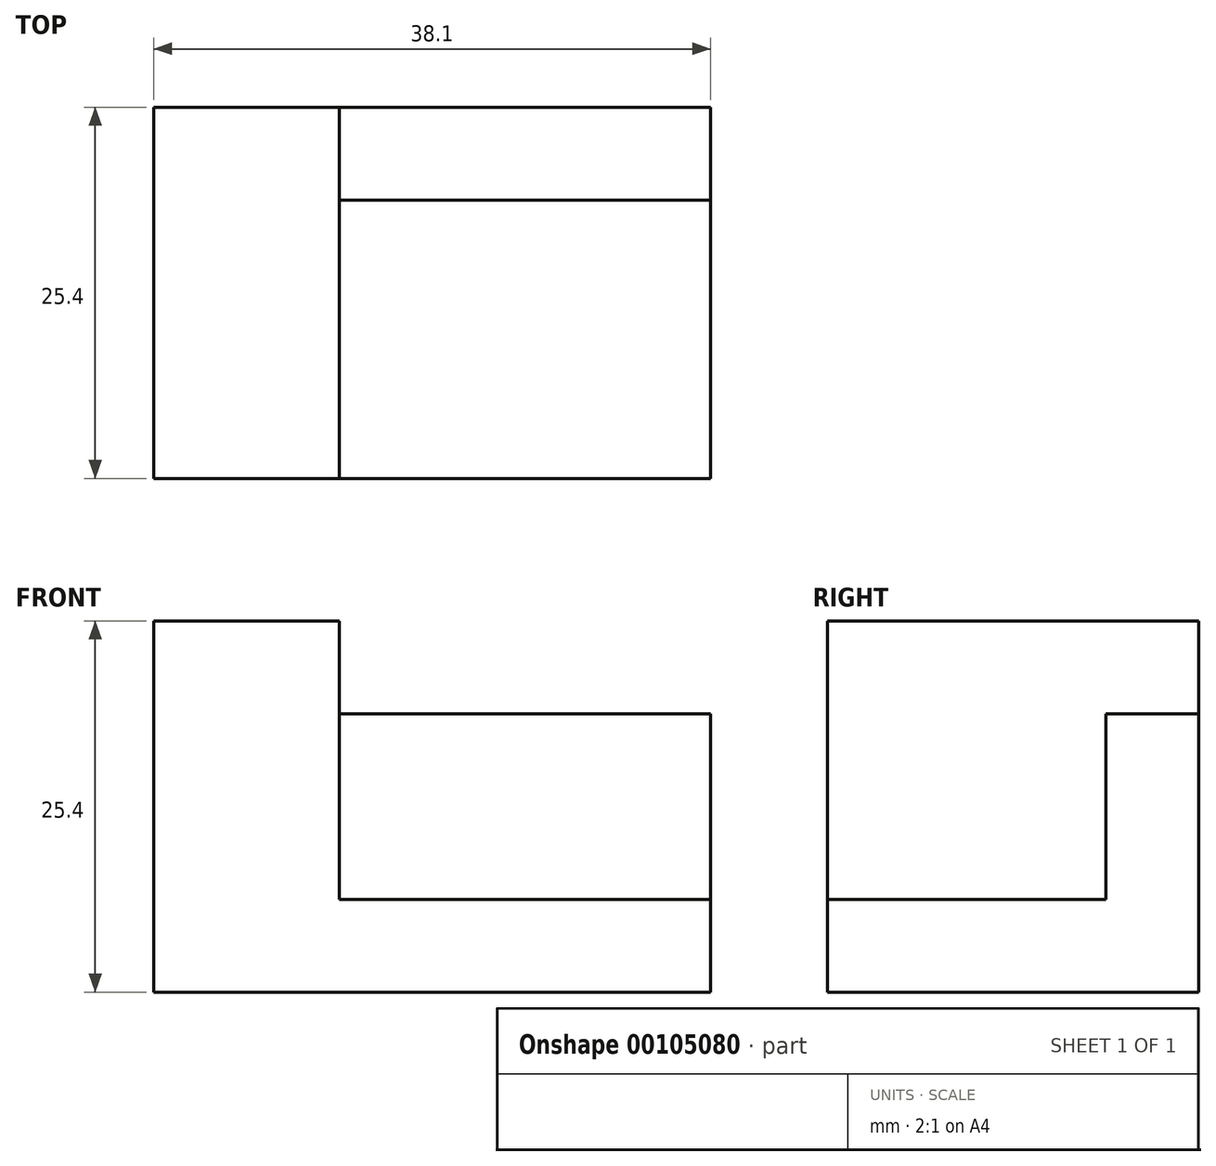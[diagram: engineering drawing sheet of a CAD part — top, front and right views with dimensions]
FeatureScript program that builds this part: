
annotation { "Feature Type Name" : "Feature", "Feature Type Description" : "" }
export const myFeature = defineFeature(function(context is Context, id is Id, definition is map)
    precondition{}
    {
        {
            var Q0;
            Q0=qCreatedBy(makeId("Front.planeOp"),FACE);
            var sketch = newSketch(context, id + "F0", { "sketchPlane" : qUnion([Q0])});
            skLineSegment(sketch, "E0", {"start": v(0, 0) * mm, "end": v(0, 25.4) * mm});
            skLineSegment(sketch, "E1", {"start": v(0, 25.4) * mm, "end": v(12.7, 25.4) * mm});
            skLineSegment(sketch, "E2", {"start": v(12.7, 25.4) * mm, "end": v(12.7, 6.35) * mm});
            skLineSegment(sketch, "E3", {"start": v(12.7, 6.35) * mm, "end": v(38.1, 6.35) * mm});
            skLineSegment(sketch, "E4", {"start": v(38.1, 6.35) * mm, "end": v(38.1, 0) * mm});
            skLineSegment(sketch, "E5", {"start": v(38.1, 0) * mm, "end": v(0, 0) * mm});
            skSolve(sketch);
        }
        {
            var Q0;
            Q0=qCreatedBy(makeId("Right.planeOp"),FACE);
            var sketch = newSketch(context, id + "F1", { "sketchPlane" : qUnion([Q0])});
            skLineSegment(sketch, "E6", {"start": v(0, 0) * mm, "end": v(0, 6.35) * mm});
            skLineSegment(sketch, "E7", {"start": v(25.4, 19.05) * mm, "end": v(25.4, 0) * mm});
            skLineSegment(sketch, "E8", {"start": v(25.4, 0) * mm, "end": v(0, 0) * mm});
            skLineSegment(sketch, "E9", {"start": v(0, 6.35) * mm, "end": v(19.05, 6.35) * mm});
            skLineSegment(sketch, "E10", {"start": v(19.05, 6.35) * mm, "end": v(19.05, 19.05) * mm});
            skLineSegment(sketch, "E11", {"start": v(19.05, 19.05) * mm, "end": v(25.4, 19.05) * mm});
            skSolve(sketch);
        }
        {
            var Q0;
            Q0=makeQuery(id+"F0.imprint","IMPRINT",FACE,{"disambiguationData":[TD([[makeQuery(id+"F0.imprint","IMPRINT",EDGE,{"derivedFrom":sQuery(id+"F0.wireOp",EDGE,"E0")}),-1.0]])]});
            extrude(context, id + "F2", {"entities" : qUnion([Q0]), "oppositeDirection" : true, "depth" : 25.4 * mm});
        }
        {
            var Q0;
            Q0=makeQuery(id+"F1.imprint","IMPRINT",FACE,{"disambiguationData":[TD([[makeQuery(id+"F1.imprint","IMPRINT",EDGE,{"derivedFrom":sQuery(id+"F1.wireOp",EDGE,"E6")}),-1.0]])]});
            extrude(context, id + "F3", {"entities" : qUnion([Q0]), "operationType" : NewBodyOperationType.ADD, "depth" : 38.1 * mm});
        }
    });
